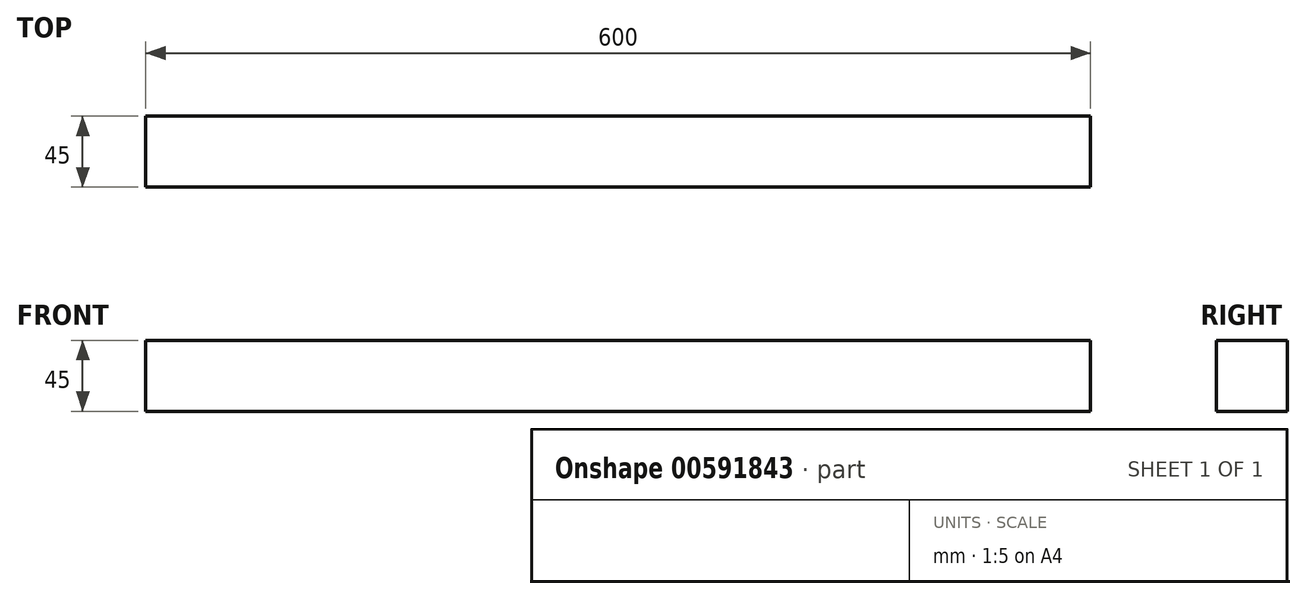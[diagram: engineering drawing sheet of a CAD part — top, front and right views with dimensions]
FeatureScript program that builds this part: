
annotation { "Feature Type Name" : "Feature", "Feature Type Description" : "" }
export const myFeature = defineFeature(function(context is Context, id is Id, definition is map)
    precondition{}
    {
        {
            var Q0;
            Q0=qCreatedBy(makeId("Right.planeOp"),FACE);
            var sketch = newSketch(context, id + "F0", { "sketchPlane" : qUnion([Q0])});
            skLineSegment(sketch, "E0.bottom", {"start": v(0, 0) * mm, "end": v(45, 0) * mm});
            skLineSegment(sketch, "E0.top", {"start": v(0, 45) * mm, "end": v(45, 45) * mm});
            skLineSegment(sketch, "E0.left", {"start": v(0, 0) * mm, "end": v(0, 45) * mm});
            skLineSegment(sketch, "E0.right", {"start": v(45, 0) * mm, "end": v(45, 45) * mm});
            skSolve(sketch);
        }
        {
            var Q0;
            Q0=makeQuery(id+"F0.imprint","IMPRINT",FACE,{"disambiguationData":[TD([[makeQuery(id+"F0.imprint","IMPRINT",EDGE,{"derivedFrom":sQuery(id+"F0.wireOp",EDGE,"E0.bottom")}),1.0]])]});
            extrude(context, id + "F1", {"entities" : qUnion([Q0]), "depth" : 600 * mm, "offsetDistance" : 25 * mm});
        }
    });
